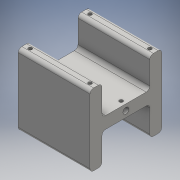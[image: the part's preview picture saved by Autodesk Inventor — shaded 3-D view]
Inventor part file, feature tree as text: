
AUTODESK INVENTOR PART (.ipt)
format: ipt  version: 2016 (Build 200138000, 138)  size: 166,912 bytes
history: native  units: mm
features: extrude x4, sketch x4, fillet x1
ambient origin geometry x8: Origin, YZ Plane, XZ Plane, XY Plane, X Axis, Y Axis, Z Axis, Center Point
bodies: Solid1 (feature_tree)
feature tree (9):
  extrude  "Block"  Depth=60.0mm
  extrude  "Motor Mount"  Depth=5.0mm
  extrude  "Plastic Savings"  Depth=5.0mm
  fillet  "Fillets FTW"  Radius=5.0mm
  extrude  "Axle Lock"  Depth=3.0mm
  sketch  "Sketch1"  dims[d0=60.0mm d1=60.0mm]
  sketch  "Sketch2"  dims[d2=5.0mm d3=5.0mm]
  sketch  "Sketch3"  dims[d4=5.0mm d5=5.0mm d6=5.0mm]
  sketch  "Sketch4"  dims[d7=5.0mm d8=5.0mm d9=5.0mm d10=3.0mm d11=3.0mm d12=3.0mm d13=3.0mm d14=60.0mm d15=0.0mm d17=5.0mm d18=60.0mm d19=0.0mm d20=10.0mm d21=10.0mm d22=5.0mm d23=5.0mm d24=60.0mm d25=0.0mm d26=3.0mm d27=4.0mm d28=3.0mm d29=3.75mm d30=0.0mm]
